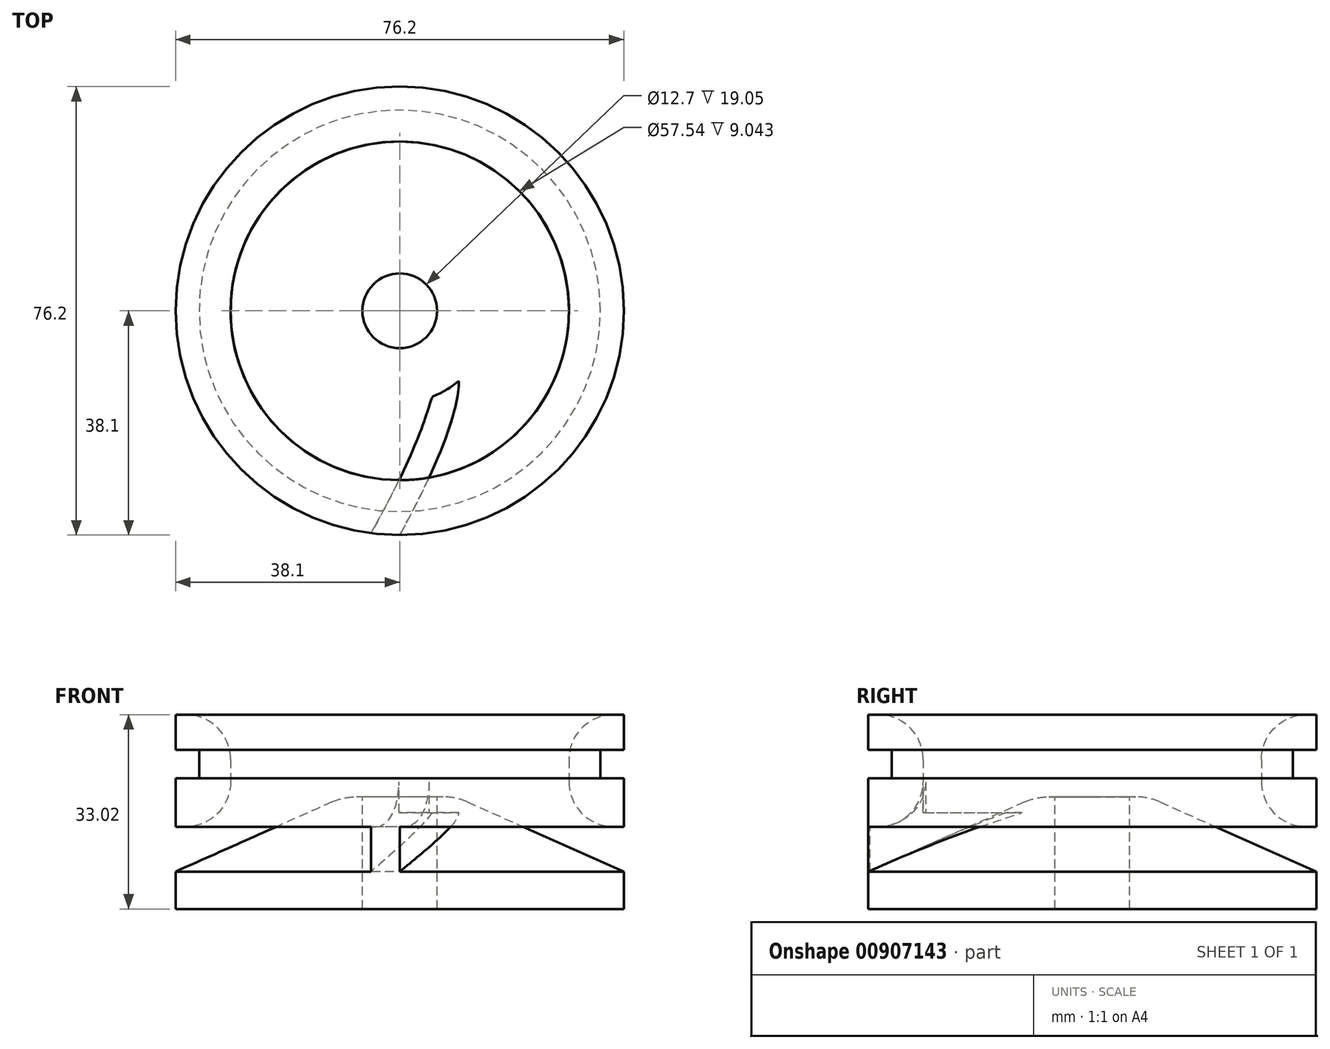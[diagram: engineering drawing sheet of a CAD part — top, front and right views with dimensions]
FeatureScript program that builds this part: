
annotation { "Feature Type Name" : "Feature", "Feature Type Description" : "" }
export const myFeature = defineFeature(function(context is Context, id is Id, definition is map)
    precondition{}
    {
        {
            var Q0;
            Q0=qCreatedBy(makeId("Top.planeOp"),FACE);
            var sketch = newSketch(context, id + "F0", { "sketchPlane" : qUnion([Q0])});
            skCircle(sketch, "E0", {"center": v(0, 0) * mm, "radius": 38.1 * mm});
            skSolve(sketch);
        }
        {
            var Q0;
            Q0=makeQuery(id+"F0.imprint","IMPRINT",FACE,{"disambiguationData":[TD([[makeQuery(id+"F0.imprint","IMPRINT",EDGE,{"derivedFrom":sQuery(id+"F0.wireOp",EDGE,"E0")}),1.0]])]});
            extrude(context, id + "F1", {"entities" : qUnion([Q0]), "depth" : 6.35 * mm, "offsetDistance" : 25.4 * mm});
        }
        {
            var Q0;
            Q0=qCreatedBy(makeId("Top.planeOp"),FACE);
            cPlane(context, id + "F2", {"entities" : qUnion([Q0]), "cplaneType" : CPlaneType.OFFSET, "offset" : 19.05 * mm, "width" : 152.4 * mm, "height" : 152.4 * mm});
        }
        {
            var Q0;
            Q0=qCreatedBy(id+"F2.planeOp",FACE);
            var sketch = newSketch(context, id + "F3", { "sketchPlane" : qUnion([Q0])});
            skCircle(sketch, "E1", {"center": v(0, 0) * mm, "radius": 9.53 * mm});
            skSolve(sketch);
        }
        {
            var Q1;
            Q1=makeQuery(id+"F1.opExtrude","CAP_FACE",FACE,{"disambiguationData":[OSD([sQuery(id+"F0.wireOp",EDGE,"E0")])],"isStart":false});
            var Q2;
            Q2=makeQuery(id+"F3.imprint","IMPRINT",FACE,{"disambiguationData":[TD([[makeQuery(id+"F3.imprint","IMPRINT",EDGE,{"derivedFrom":sQuery(id+"F3.wireOp",EDGE,"E1")}),1.0]])]});
            loft(context, id + "F4", {"operationType" : NewBodyOperationType.ADD, "sheetProfilesArray" : [{ "sheetProfileEntities" : qUnion([Q1]) }, { "sheetProfileEntities" : qUnion([Q2]) }]});
        }
        {
            var Q0;
            Q0=makeQuery(id+"F4.opLoft","CAP_FACE",FACE,{"disambiguationData":[OSD([makeQuery(id+"F3.imprint","IMPRINT",FACE,{"disambiguationData":[TD([[makeQuery(id+"F3.imprint","IMPRINT",EDGE,{"derivedFrom":sQuery(id+"F3.wireOp",EDGE,"E1")}),1.0]])]})])],"isStart":true});
            var sketch = newSketch(context, id + "F5", { "sketchPlane" : qUnion([Q0])});
            skCircle(sketch, "E2", {"center": v(0, 0) * mm, "radius": 6.35 * mm});
            skSolve(sketch);
        }
        {
            var Q0;
            Q0 = qSketchRegion(id + "F5", true);
            extrude(context, id + "F6", {"entities" : qUnion([Q0]), "operationType" : NewBodyOperationType.REMOVE, "endBound" : BoundingType.THROUGH_ALL, "oppositeDirection" : true, "depth" : 25.4 * mm, "offsetDistance" : 25.4 * mm});
        }
        {
            var Q0;
            Q0=makeQuery(id+"F4.opLoft","MID_CAP_EDGE",EDGE,{"disambiguationData":[OSD([sQuery(id+"F3.wireOp",EDGE,"E1")])],"capPos":1.0});
            fillet(context, id + "F7", {"entities" : qUnion([Q0]), "radius" : 10.16 * mm, "tangentPropagation" : true, "allowEdgeOverflow" : false});
        }
        {
            var Q0;
            Q0=qCreatedBy(makeId("Front.planeOp"),FACE);
            cPlane(context, id + "F8", {"entities" : qUnion([Q0]), "cplaneType" : CPlaneType.OFFSET, "offset" : 38.1 * mm, "width" : 152.4 * mm, "height" : 152.4 * mm});
        }
        {
            var Q0;
            Q0=qCreatedBy(id+"F8.planeOp",FACE);
            var sketch = newSketch(context, id + "F9", { "sketchPlane" : qUnion([Q0])});
            skLineSegment(sketch, "E3.bottom", {"start": v(0, 6.2) * mm, "end": v(-5.08, 6.2) * mm});
            skLineSegment(sketch, "E3.top", {"start": v(0, 16.36) * mm, "end": v(-5.08, 16.36) * mm});
            skLineSegment(sketch, "E3.left", {"start": v(0, 6.2) * mm, "end": v(0, 16.36) * mm});
            skLineSegment(sketch, "E3.right", {"start": v(-5.08, 6.2) * mm, "end": v(-5.08, 16.36) * mm});
            skSolve(sketch);
        }
        {
            var Q0;
            Q0=qCreatedBy(id+"F2.planeOp",FACE);
            cPlane(context, id + "F10", {"entities" : qUnion([Q0]), "cplaneType" : CPlaneType.OFFSET, "offset" : 2.54 * mm, "oppositeDirection" : true, "width" : 152.4 * mm, "height" : 152.4 * mm});
        }
        {
            var Q0;
            Q0=qCreatedBy(id+"F10.planeOp",FACE);
            var sketch = newSketch(context, id + "F11", { "sketchPlane" : qUnion([Q0])});
            skFitSpline(sketch, "E4", {"points": [v(0, -38.1) * mm, v(8.72, -18.9) * mm, v(10.01, -11.57) * mm], "startDerivative": vector(19.21, 34.94) * mm, "endDerivative": vector(-1.17, 12.65) * mm});
            skSolve(sketch);
        }
        {
            var Q0;
            Q0=makeQuery(id+"F9.imprint","IMPRINT",FACE,{"disambiguationData":[TD([[makeQuery(id+"F9.imprint","IMPRINT",EDGE,{"derivedFrom":sQuery(id+"F9.wireOp",EDGE,"E3.bottom")}),-1.0]])]});
            var Q1;
            Q1=sQuery(id+"F11.wireOp",EDGE,"E4");
            sweep(context, id + "F12", {"operationType" : NewBodyOperationType.ADD, "profiles" : qUnion([Q0]), "path" : qUnion([Q1])});
        }
        {
            var Q0;
            Q0=qCreatedBy(id+"F2.planeOp",FACE);
            var sketch = newSketch(context, id + "F13", { "sketchPlane" : qUnion([Q0])});
            skCircle(sketch, "E5", {"center": v(0, 0) * mm, "radius": 38.1 * mm});
            skSolve(sketch);
        }
        {
            var Q0;
            Q0 = qSketchRegion(id + "F13", true);
            extrude(context, id + "F14", {"entities" : qUnion([Q0]), "operationType" : NewBodyOperationType.INTERSECT, "oppositeDirection" : true, "depth" : 25.4 * mm, "offsetDistance" : 25.4 * mm});
        }
        {
            var Q0;
            Q0=qCreatedBy(id+"F10.planeOp",FACE);
            cPlane(context, id + "F15", {"entities" : qUnion([Q0]), "cplaneType" : CPlaneType.OFFSET, "offset" : 2.54 * mm, "oppositeDirection" : true, "width" : 152.4 * mm, "height" : 152.4 * mm});
        }
        {
            var Q0;
            Q0=qCreatedBy(id+"F15.planeOp",FACE);
            var sketch = newSketch(context, id + "F16", { "sketchPlane" : qUnion([Q0])});
            skCircle(sketch, "E6", {"center": v(0, 0) * mm, "radius": 38.1 * mm});
            skCircle(sketch, "E7", {"center": v(0, 0) * mm, "radius": 28.77 * mm});
            skSolve(sketch);
        }
        {
            var Q0;
            Q0 = qSketchRegion(id + "F16", true);
            extrude(context, id + "F17", {"entities" : qUnion([Q0]), "operationType" : NewBodyOperationType.ADD, "depth" : 19.05 * mm, "offsetDistance" : 25.4 * mm});
        }
        {
            var Q0;
            {var subQ0=sQuery(id+"F11.wireOp",EDGE,"E4");var subQ1=sQuery(id+"F16.wireOp",EDGE,"E7");Q0=makeQuery(id+"F17.boolean.opBoolean","SPLIT",EDGE,{"disambiguationData":[TD([makeQuery(id+"FxxrDtunKPFlRTC_1.2.F12.opSweep","SWEPT_FACE",FACE,{"disambiguationData":[OSD([sQuery(id+"F9.wireOp",EDGE,"E3.right"),subQ0])]})])],"derivedFrom":makeQuery(id+"F17.opExtrude","CAP_EDGE",EDGE,{"disambiguationData":[OSD([subQ1])],"isStart":true})});}
            var Q1;
            {var subQ0=sQuery(id+"F11.wireOp",EDGE,"E4");var subQ1=sQuery(id+"F16.wireOp",EDGE,"E7");Q1=makeQuery(id+"F17.boolean.opBoolean","SPLIT",EDGE,{"disambiguationData":[TD([makeQuery(id+"FxxrDtunKPFlRTC_1.3.F12.opSweep","SWEPT_FACE",FACE,{"disambiguationData":[OSD([sQuery(id+"F9.wireOp",EDGE,"E3.right"),subQ0])]})])],"derivedFrom":makeQuery(id+"F17.opExtrude","CAP_EDGE",EDGE,{"disambiguationData":[OSD([subQ1])],"isStart":true})});}
            var Q2;
            Q2=makeQuery(id+"F17.opExtrude","CAP_EDGE",EDGE,{"disambiguationData":[OSD([sQuery(id+"F16.wireOp",EDGE,"E7")])],"isStart":false});
            var Q3;
            {var subQ0=sQuery(id+"F11.wireOp",EDGE,"E4");var subQ1=sQuery(id+"F16.wireOp",EDGE,"E7");Q3=makeQuery(id+"F17.boolean.opBoolean","SPLIT",EDGE,{"disambiguationData":[TD([makeQuery(id+"FxxrDtunKPFlRTC_1.1.F12.opSweep","SWEPT_FACE",FACE,{"disambiguationData":[OSD([sQuery(id+"F9.wireOp",EDGE,"E3.right"),subQ0])]})])],"derivedFrom":makeQuery(id+"F17.opExtrude","CAP_EDGE",EDGE,{"disambiguationData":[OSD([subQ1])],"isStart":true})});}
            var Q4;
            {var subQ0=sQuery(id+"F11.wireOp",EDGE,"E4");var subQ1=sQuery(id+"F16.wireOp",EDGE,"E7");Q4=makeQuery(id+"F17.boolean.opBoolean","SPLIT",EDGE,{"disambiguationData":[TD([makeQuery(id+"F12.opSweep","SWEPT_FACE",FACE,{"disambiguationData":[OSD([sQuery(id+"F9.wireOp",EDGE,"E3.right"),subQ0])]})])],"derivedFrom":makeQuery(id+"F17.opExtrude","CAP_EDGE",EDGE,{"disambiguationData":[OSD([subQ1])],"isStart":true})});}
            var Q5;
            {var subQ0=sQuery(id+"F11.wireOp",EDGE,"E4");var subQ1=sQuery(id+"F16.wireOp",EDGE,"E7");Q5=makeQuery(id+"F17.boolean.opBoolean","SPLIT",EDGE,{"disambiguationData":[TD([makeQuery(id+"FxxrDtunKPFlRTC_1.4.F12.opSweep","SWEPT_FACE",FACE,{"disambiguationData":[OSD([sQuery(id+"F9.wireOp",EDGE,"E3.right"),subQ0])]})])],"derivedFrom":makeQuery(id+"F17.opExtrude","CAP_EDGE",EDGE,{"disambiguationData":[OSD([subQ1])],"isStart":true})});}
            var Q6;
            {var subQ0=sQuery(id+"F11.wireOp",EDGE,"E4");var subQ1=sQuery(id+"F16.wireOp",EDGE,"E7");Q6=makeQuery(id+"F17.boolean.opBoolean","SPLIT",EDGE,{"disambiguationData":[TD([makeQuery(id+"FxxrDtunKPFlRTC_1.5.F12.opSweep","SWEPT_FACE",FACE,{"disambiguationData":[OSD([sQuery(id+"F9.wireOp",EDGE,"E3.right"),subQ0])]})])],"derivedFrom":makeQuery(id+"F17.opExtrude","CAP_EDGE",EDGE,{"disambiguationData":[OSD([subQ1])],"isStart":true})});}
            var Q7;
            {var subQ0=sQuery(id+"F11.wireOp",EDGE,"E4");var subQ1=sQuery(id+"F16.wireOp",EDGE,"E7");Q7=makeQuery(id+"F17.boolean.opBoolean","SPLIT",EDGE,{"disambiguationData":[TD([makeQuery(id+"FxxrDtunKPFlRTC_1.6.F12.opSweep","SWEPT_FACE",FACE,{"disambiguationData":[OSD([sQuery(id+"F9.wireOp",EDGE,"E3.right"),subQ0])]})])],"derivedFrom":makeQuery(id+"F17.opExtrude","CAP_EDGE",EDGE,{"disambiguationData":[OSD([subQ1])],"isStart":true})});}
            var Q8;
            {var subQ0=sQuery(id+"F11.wireOp",EDGE,"E4");var subQ1=sQuery(id+"F16.wireOp",EDGE,"E7");Q8=makeQuery(id+"F17.boolean.opBoolean","SPLIT",EDGE,{"disambiguationData":[TD([makeQuery(id+"F12.opSweep","SWEPT_FACE",FACE,{"disambiguationData":[OSD([sQuery(id+"F9.wireOp",EDGE,"E3.left"),subQ0])]})])],"derivedFrom":makeQuery(id+"F17.opExtrude","CAP_EDGE",EDGE,{"disambiguationData":[OSD([subQ1])],"isStart":true})});}
            fillet(context, id + "F18", {"entities" : qUnion([Q0, Q1, Q2, Q3, Q4, Q5, Q6, Q7, Q8]), "radius" : 7.62 * mm, "tangentPropagation" : true, "allowEdgeOverflow" : false});
        }
        {
            var Q0;
            Q0=qCreatedBy(makeId("Front.planeOp"),FACE);
            var sketch = newSketch(context, id + "F19", { "sketchPlane" : qUnion([Q0])});
            skLineSegment(sketch, "E8.bottom", {"start": v(34.1, 27.05) * mm, "end": v(38.17, 27.05) * mm});
            skLineSegment(sketch, "E8.top", {"start": v(34.1, 22.23) * mm, "end": v(38.17, 22.23) * mm});
            skLineSegment(sketch, "E8.left", {"start": v(34.1, 27.05) * mm, "end": v(34.1, 22.23) * mm});
            skLineSegment(sketch, "E8.right", {"start": v(38.17, 27.05) * mm, "end": v(38.17, 22.23) * mm});
            skSolve(sketch);
        }
        {
            var Q0;
            Q0 = qSketchRegion(id + "F19", true);
            var Q1;
            Q1=makeQuery(id+"F6.boolean.opBoolean","COPY",FACE,{"derivedFrom":makeQuery(id+"F6.opExtrude","SWEPT_FACE",FACE,{"disambiguationData":[OSD([sQuery(id+"F5.wireOp",EDGE,"E2")])]})});
            revolve(context, id + "F20", {"operationType" : NewBodyOperationType.REMOVE, "surfaceOperationType" : NewSurfaceOperationType.NEW, "entities" : qUnion([Q0]), "axis" : qUnion([Q1]), "revolveType" : RevolveType.FULL, "oppositeDirection" : true});
        }
    });
